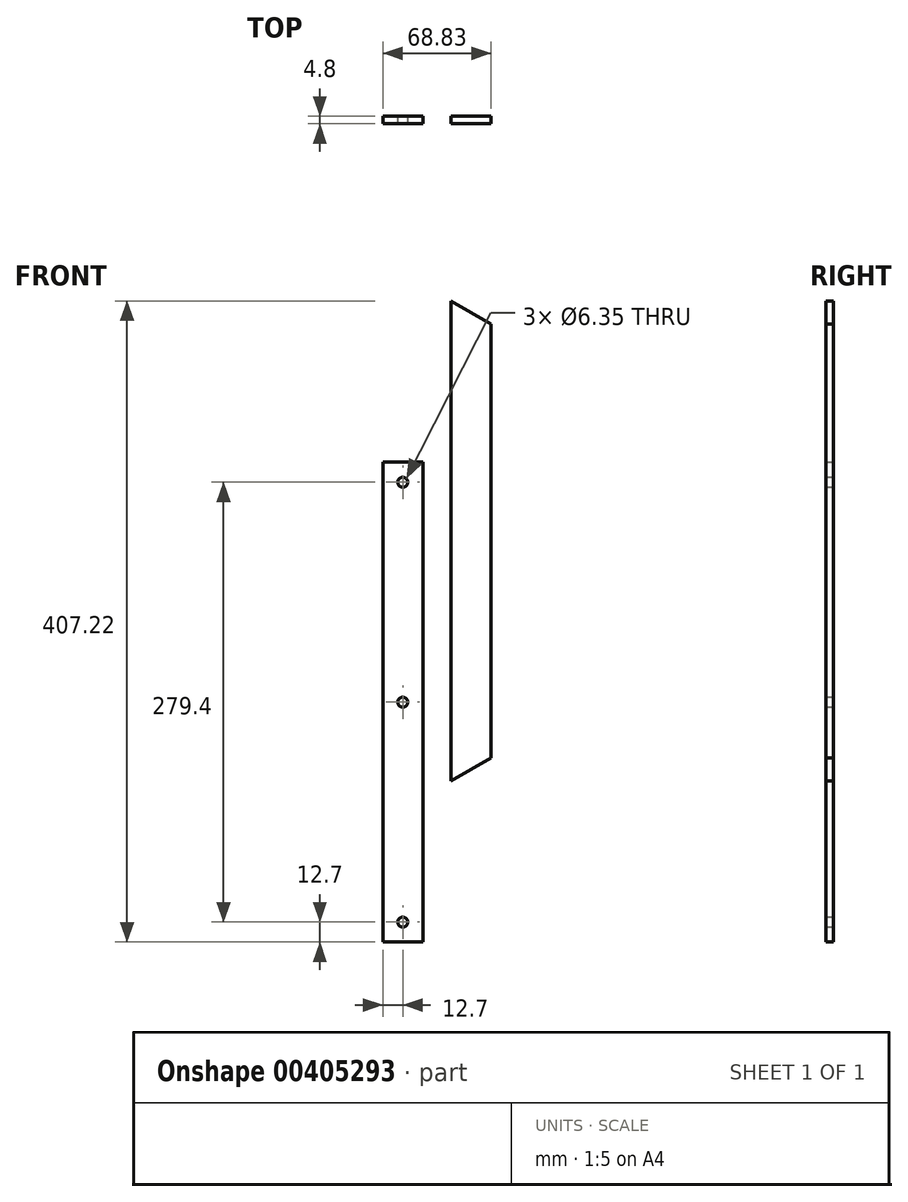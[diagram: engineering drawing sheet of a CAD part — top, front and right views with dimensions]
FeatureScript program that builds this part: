
annotation { "Feature Type Name" : "Feature", "Feature Type Description" : "" }
export const myFeature = defineFeature(function(context is Context, id is Id, definition is map)
    precondition{}
    {
        {
            var Q0;
            Q0=qCreatedBy(makeId("Front.planeOp"),FACE);
            var sketch = newSketch(context, id + "F0", { "sketchPlane" : qUnion([Q0])});
            skLineSegment(sketch, "E0.bottom", {"start": v(12.7, -152.4) * mm, "end": v(-12.7, -152.4) * mm});
            skLineSegment(sketch, "E0.top", {"start": v(12.7, 152.4) * mm, "end": v(-12.7, 152.4) * mm});
            skLineSegment(sketch, "E0.left", {"start": v(12.7, -152.4) * mm, "end": v(12.7, 152.4) * mm});
            skLineSegment(sketch, "E0.right", {"start": v(-12.7, -152.4) * mm, "end": v(-12.7, 152.4) * mm});
            skPoint(sketch, "E0.middle", {"position": v(0, 0) * mm});
            skCircle(sketch, "E1", {"center": v(0, 139.7) * mm, "radius": 3.18 * mm});
            skLineSegment(sketch, "E2", {"start": v(0, 0) * mm, "end": v(12.7, 0) * mm, "construction": true});
            skCircle(sketch, "E3.MirrorC", {"center": v(0, -139.7) * mm, "radius": 3.18 * mm});
            skCircle(sketch, "E4", {"center": v(0, 0) * mm, "radius": 3.18 * mm});
            skSolve(sketch);
        }
        {
            var Q0;
            Q0=makeQuery(id+"F0.imprint","IMPRINT",FACE,{"disambiguationData":[TD([[makeQuery(id+"F0.imprint","IMPRINT",EDGE,{"derivedFrom":sQuery(id+"F0.wireOp",EDGE,"E0.bottom")}),-1.0]])]});
            extrude(context, id + "F1", {"entities" : qUnion([Q0]), "depth" : 4.8 * mm});
        }
        {
            var Q0;
            Q0=qCreatedBy(makeId("Front.planeOp"),FACE);
            var sketch = newSketch(context, id + "F2", { "sketchPlane" : qUnion([Q0])});
            skLineSegment(sketch, "E5", {"start": v(30.73, 254.82) * mm, "end": v(30.73, -49.98) * mm});
            skLineSegment(sketch, "E6", {"start": v(30.73, -49.98) * mm, "end": v(56.13, -35.31) * mm});
            skLineSegment(sketch, "E7", {"start": v(56.13, -35.31) * mm, "end": v(56.13, 240.16) * mm});
            skLineSegment(sketch, "E8", {"start": v(56.13, 240.16) * mm, "end": v(30.73, 254.82) * mm});
            skSolve(sketch);
        }
        {
            var Q0;
            Q0=makeQuery(id+"F2.imprint","IMPRINT",FACE,{"disambiguationData":[TD([[makeQuery(id+"F2.imprint","IMPRINT",EDGE,{"derivedFrom":sQuery(id+"F2.wireOp",EDGE,"E5")}),1.0]])]});
            var Q1;
            Q1=makeQuery(id+"F1.opExtrude","CAP_FACE",FACE,{"disambiguationData":[OSD([sQuery(id+"F0.wireOp",EDGE,"E0.bottom"),sQuery(id+"F0.wireOp",EDGE,"E0.top"),sQuery(id+"F0.wireOp",EDGE,"E0.left"),sQuery(id+"F0.wireOp",EDGE,"E0.right"),sQuery(id+"F0.wireOp",EDGE,"E1"),sQuery(id+"F0.wireOp",EDGE,"E3.MirrorC"),sQuery(id+"F0.wireOp",EDGE,"E4")])],"isStart":false});
            extrude(context, id + "F3", {"entities" : qUnion([Q0]), "endBound" : BoundingType.UP_TO_SURFACE, "endBoundEntityFace" : qUnion([Q1]), "depth" : 25.4 * mm});
        }
    });
